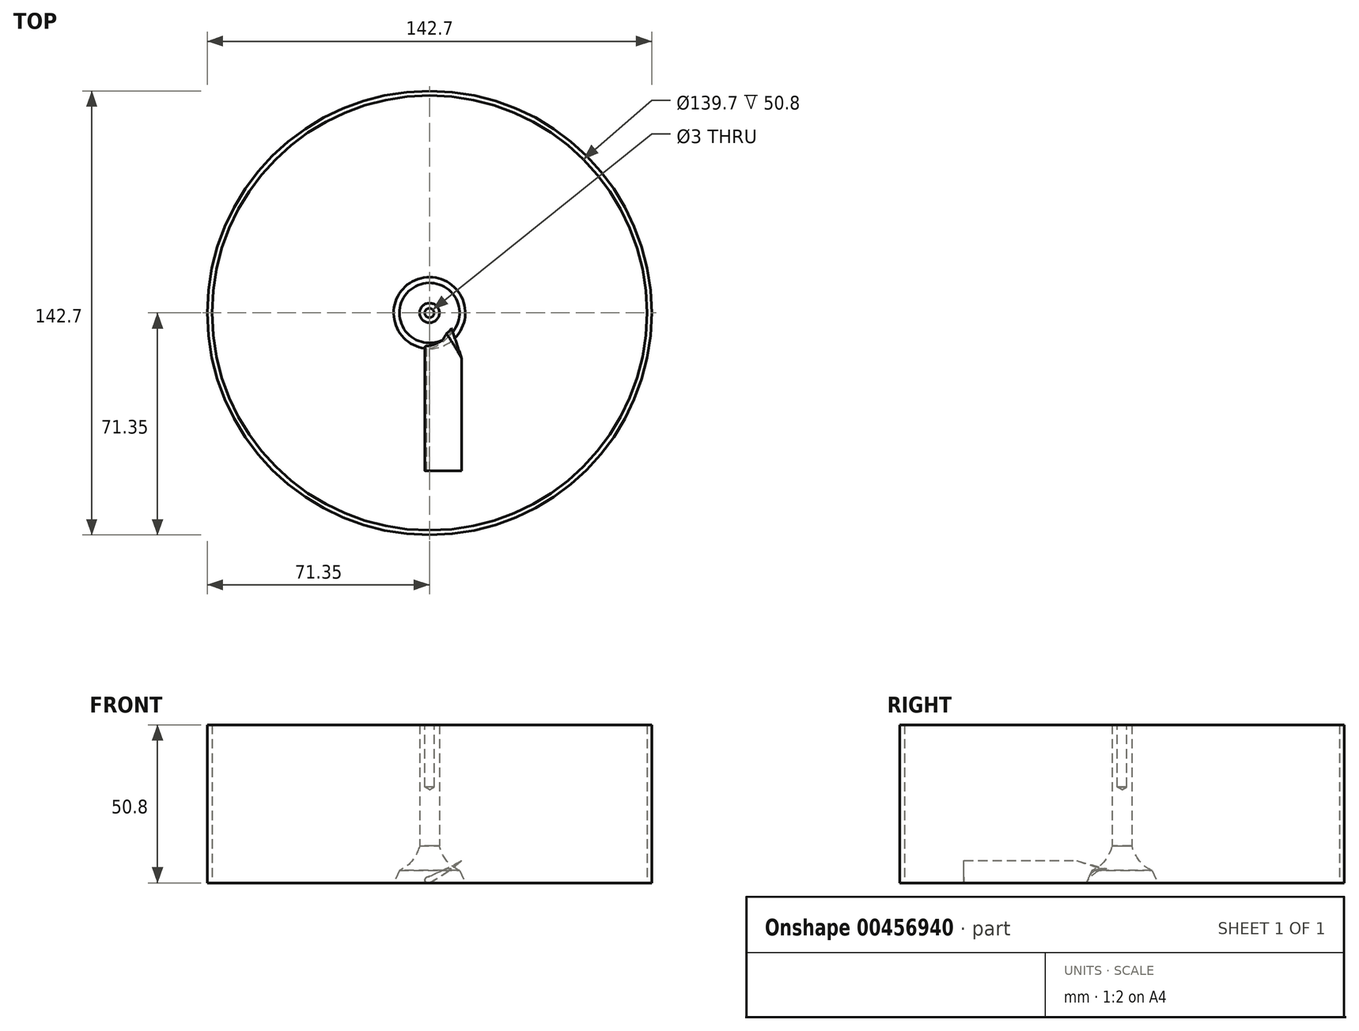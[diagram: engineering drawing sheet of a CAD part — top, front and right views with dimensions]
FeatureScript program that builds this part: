
annotation { "Feature Type Name" : "Feature", "Feature Type Description" : "" }
export const myFeature = defineFeature(function(context is Context, id is Id, definition is map)
    precondition{}
    {
        {
            var Q0;
            Q0=qCreatedBy(makeId("Front.planeOp"),FACE);
            var sketch = newSketch(context, id + "F0", { "sketchPlane" : qUnion([Q0])});
            skLineSegment(sketch, "E0", {"start": v(0, 0) * mm, "end": v(11, 6.35) * mm, "construction": true});
            skLineSegment(sketch, "E1", {"start": v(0, 0) * mm, "end": v(3.86, 0) * mm, "construction": true});
            skLineSegment(sketch, "E2.0", {"start": v(-0.62, 0.8) * mm, "end": v(10.38, 7.14) * mm, "construction": true});
            skFitSpline(sketch, "E3", {"points": [v(0, 0) * mm, v(2.62, 1.51) * mm, v(7.27, 4.68) * mm, v(10.38, 7.14) * mm], "startDerivative": vector(8.9, 4.4) * mm, "endDerivative": vector(8.82, 7.21) * mm});
            skLineSegment(sketch, "E4.0", {"start": v(-0.75, 1.88) * mm, "end": v(9.88, 8.01) * mm, "construction": true});
            skFitSpline(sketch, "E5", {"points": [v(-0.75, 1.88) * mm, v(2.33, 3.15) * mm, v(6.1, 4.85) * mm, v(10.38, 7.14) * mm], "startDerivative": vector(11.35, 3.56) * mm, "endDerivative": vector(12.14, 6.7) * mm});
            skArc(sketch, "E6", {"start": v(-0.75, 1.88) * mm, "mid": v(-1.39, 0.53) * mm, "end": v(0, 0) * mm});
            skLineSegment(sketch, "E7", {"start": v(0, 0) * mm, "end": v(0, 29.65) * mm, "construction": true});
            skSolve(sketch);
        }
        {
            var Q0;
            Q0=qSketchRegion(id+"F0",true);
            extrude(context, id + "F1", {"entities" : qUnion([Q0]), "depth" : 50.8 * mm});
        }
        {
            var Q0;
            Q0=qCreatedBy(makeId("Front.planeOp"),FACE);
            var sketch = newSketch(context, id + "F2", { "sketchPlane" : qUnion([Q0])});
            skLineSegment(sketch, "E8", {"start": v(0, 2.13) * mm, "end": v(20.26, 7.8) * mm});
            skLineSegment(sketch, "E9", {"start": v(20.26, 7.8) * mm, "end": v(0, 7.8) * mm});
            skLineSegment(sketch, "E10", {"start": v(0, 7.8) * mm, "end": v(0, 2.13) * mm});
            skSolve(sketch);
        }
        {
            var Q0;
            Q0=qSketchRegion(id+"F2",true);
            var Q1;
            Q1=sQuery(id+"F0.wireOp",EDGE,"E7");
            revolve(context, id + "F3", {"operationType" : NewBodyOperationType.REMOVE, "entities" : qUnion([Q0]), "axis" : qUnion([Q1]), "revolveType" : RevolveType.FULL, "oppositeDirection" : true});
        }
        {
            var Q0;
            Q0=qCreatedBy(makeId("Top.planeOp"),FACE);
            var sketch = newSketch(context, id + "F4", { "sketchPlane" : qUnion([Q0])});
            skCircle(sketch, "E11", {"center": v(0, 0) * mm, "radius": 3.18 * mm});
            skSolve(sketch);
        }
        {
            var Q0;
            Q0=qSketchRegion(id+"F4",true);
            extrude(context, id + "F5", {"entities" : qUnion([Q0]), "operationType" : NewBodyOperationType.ADD, "depth" : 50.8 * mm});
        }
        {
            var Q0;
            Q0=qCreatedBy(makeId("Right.planeOp"),FACE);
            var sketch = newSketch(context, id + "F6", { "sketchPlane" : qUnion([Q0])});
            skLineSegment(sketch, "E12", {"start": v(0, 0) * mm, "end": v(-254, 0) * mm});
            skLineSegment(sketch, "E13.0", {"start": v(0, -23) * mm, "end": v(-254, -23) * mm});
            skLineSegment(sketch, "E14", {"start": v(-254, -23) * mm, "end": v(-254, 0) * mm});
            skLineSegment(sketch, "E15", {"start": v(0, -23) * mm, "end": v(0, 0) * mm});
            skSolve(sketch);
        }
        {
            var Q0;
            Q0=qSketchRegion(id+"F6",true);
            var Q1;
            Q1=qConstructionFilter(qBodyType(qCreatedBy(id+"F6",EDGE),BodyType.WIRE),ConstructionObject.NO);
            var Q2;
            Q2=sQuery(id+"F0.wireOp",EDGE,"E7");
            revolve(context, id + "F7", {"operationType" : NewBodyOperationType.REMOVE, "entities" : qUnion([Q0]), "surfaceEntities" : qUnion([Q1]), "axis" : qUnion([Q2]), "revolveType" : RevolveType.FULL});
        }
        {
            var Q0;
            Q0=qCreatedBy(makeId("Right.planeOp"),FACE);
            var sketch = newSketch(context, id + "F8", { "sketchPlane" : qUnion([Q0])});
            skLineSegment(sketch, "E16", {"start": v(-11.5, 0) * mm, "end": v(-1.5, 0) * mm});
            skLineSegment(sketch, "E17", {"start": v(-1.5, 0) * mm, "end": v(-1.5, 12.5) * mm});
            skLineSegment(sketch, "E18", {"start": v(-1.5, 12.5) * mm, "end": v(-3, 12.5) * mm});
            skFitSpline(sketch, "E19", {"points": [v(-3, 12.5) * mm, v(-4.7, 8.33) * mm, v(-6.96, 5.64) * mm, v(-9.65, 3.97) * mm], "startDerivative": vector(-3, -12.47) * mm, "endDerivative": vector(-9.37, -4.97) * mm});
            skLineSegment(sketch, "E20", {"start": v(-9.65, 3.97) * mm, "end": v(-11.5, 0) * mm});
            skSolve(sketch);
        }
        {
            var Q0;
            Q0=qSketchRegion(id+"F8",true);
            var Q1;
            Q1=sQuery(id+"F0.wireOp",EDGE,"E7");
            revolve(context, id + "F9", {"operationType" : NewBodyOperationType.ADD, "entities" : qUnion([Q0]), "axis" : qUnion([Q1]), "revolveType" : RevolveType.FULL});
        }
        {
            var Q0;
            Q0=qCreatedBy(makeId("Top.planeOp"),FACE);
            var sketch = newSketch(context, id + "F10", { "sketchPlane" : qUnion([Q0])});
            skCircle(sketch, "E21", {"center": v(0, 0) * mm, "radius": 69.85 * mm});
            skCircle(sketch, "E22.0", {"center": v(0, 0) * mm, "radius": 71.35 * mm});
            skSolve(sketch);
        }
        {
            var Q0;
            Q0=qSketchRegion(id+"F10",true);
            extrude(context, id + "F11", {"entities" : qUnion([Q0]), "operationType" : NewBodyOperationType.ADD, "depth" : 50.8 * mm});
        }
        {
            var Q0;
            Q0=makeQuery(id+"F5.opExtrude","CAP_FACE",FACE,{"disambiguationData":[OSD([sQuery(id+"F4.wireOp",EDGE,"E11")])],"isStart":false});
            var sketch = newSketch(context, id + "F12", { "sketchPlane" : qUnion([Q0])});
            skPoint(sketch, "E23", {"position": v(0, 0) * mm});
            skSolve(sketch);
        }
        {
            var Q0;
            Q0=sQuery(id+"F12.wireOp",VERTEX,"E23");
            var Q1;
            Q1=makeQuery(id+"F1.opExtrude","SWEPT_BODY",BODY,{"disambiguationData":[OSD([sQuery(id+"F0.wireOp",EDGE,"E3"),sQuery(id+"F0.wireOp",EDGE,"E5"),sQuery(id+"F0.wireOp",EDGE,"E6")])]});
            hole(context, id + "F13", {"style" : HoleStyle.SIMPLE, "endStyle" : HoleEndStyle.BLIND, "holeDiameter" : 3 * mm, "holeDepth" : 20 * mm, "locations" : qUnion([Q0]), "scope" : qUnion([Q1])});
        }
    });
